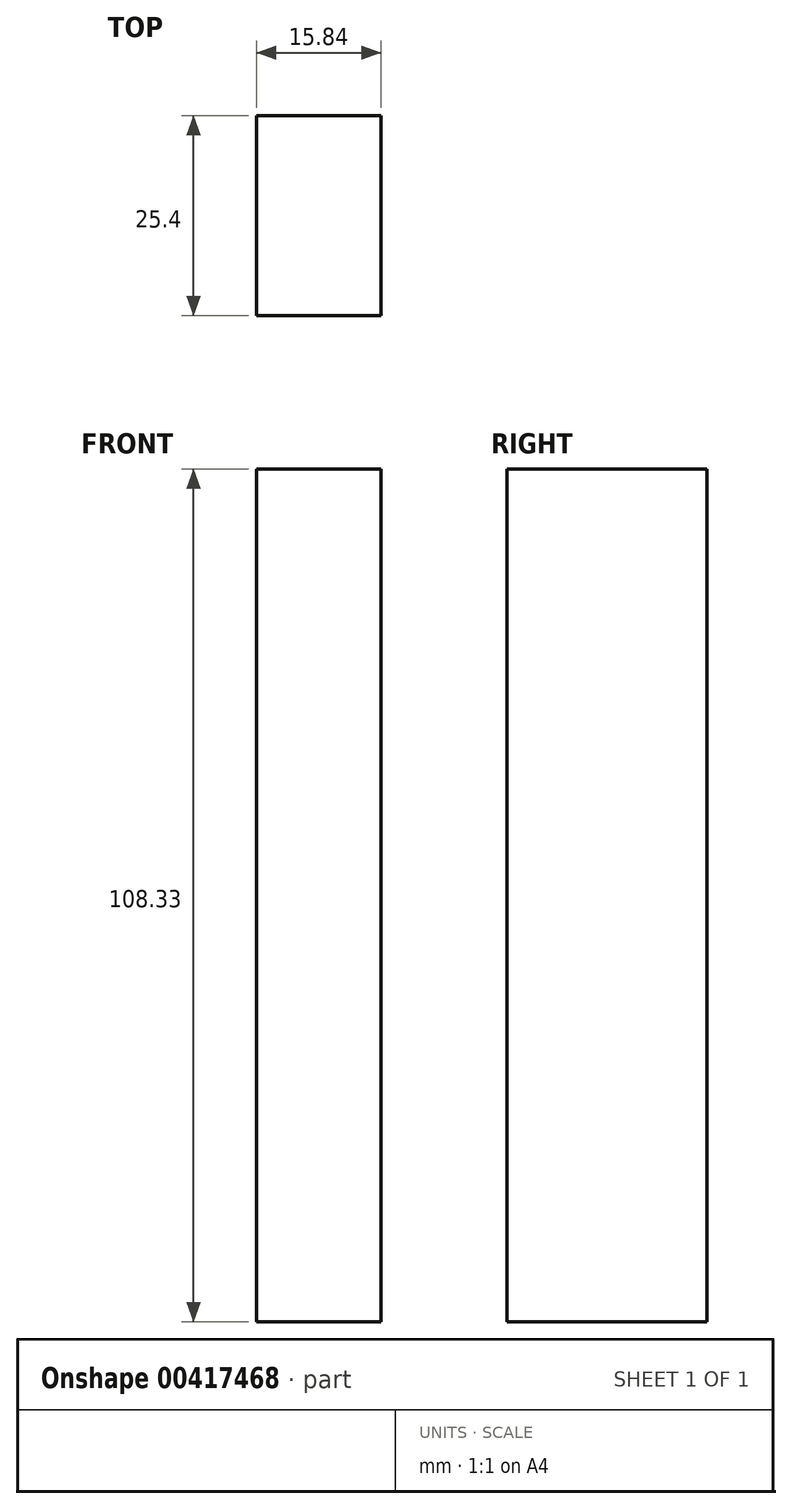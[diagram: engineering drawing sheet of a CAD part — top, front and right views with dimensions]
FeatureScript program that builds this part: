
annotation { "Feature Type Name" : "Feature", "Feature Type Description" : "" }
export const myFeature = defineFeature(function(context is Context, id is Id, definition is map)
    precondition{}
    {
        {
            var Q0;
            Q0=qCreatedBy(makeId("Front.planeOp"),FACE);
            var sketch = newSketch(context, id + "F0", { "sketchPlane" : qUnion([Q0])});
            skLineSegment(sketch, "E0.bottom", {"start": v(0, 42.68) * mm, "end": v(-15.84, 42.68) * mm});
            skLineSegment(sketch, "E0.top", {"start": v(0, 151) * mm, "end": v(-15.84, 151) * mm});
            skLineSegment(sketch, "E0.left", {"start": v(0, 42.68) * mm, "end": v(0, 151) * mm});
            skLineSegment(sketch, "E0.right", {"start": v(-15.84, 42.68) * mm, "end": v(-15.84, 151) * mm});
            skSolve(sketch);
        }
        {
            var Q0;
            Q0 = qSketchRegion(id + "F0", true);
            extrude(context, id + "F1", {"entities" : qUnion([Q0]), "depth" : 25.4 * mm});
        }
    });
